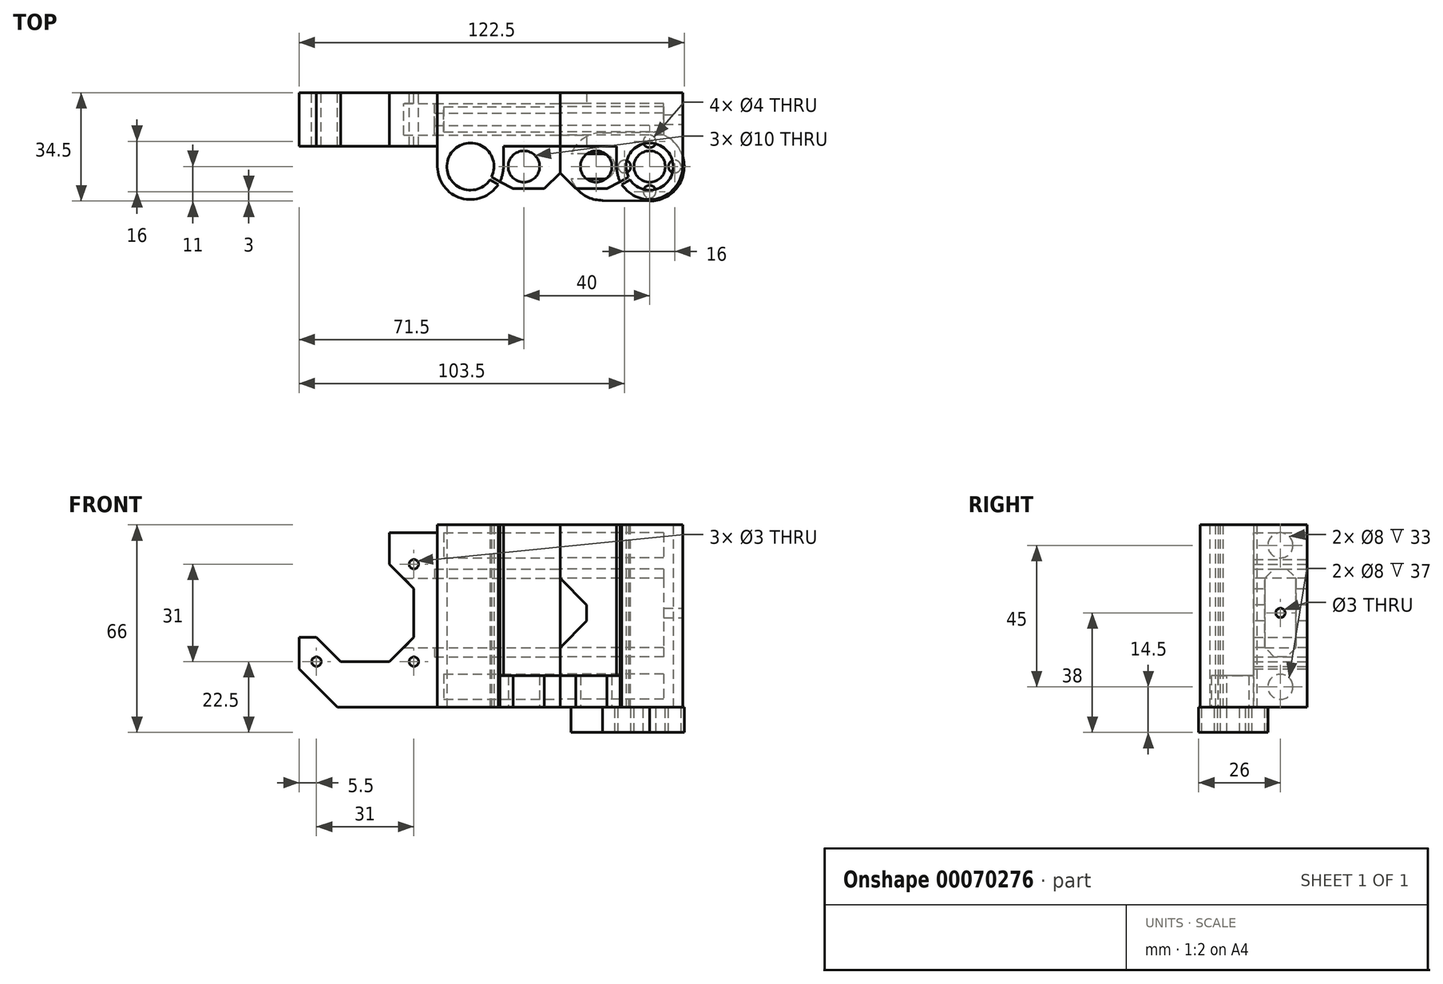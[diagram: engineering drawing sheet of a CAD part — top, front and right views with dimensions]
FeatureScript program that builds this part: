
annotation { "Feature Type Name" : "Feature", "Feature Type Description" : "" }
export const myFeature = defineFeature(function(context is Context, id is Id, definition is map)
    precondition{}
    {
        {
            var Q0;
            Q0=qCreatedBy(makeId("Top.planeOp"),FACE);
            var sketch = newSketch(context, id + "F0", { "sketchPlane" : qUnion([Q0])});
            skCircle(sketch, "E0", {"center": v(-17, 0) * mm, "radius": 5 * mm, "construction": true});
            skArc(sketch, "E1", {"start": v(-10.5, 0) * mm, "mid": v(-10.2, -2.48) * mm, "end": v(-9.33, -4.81) * mm});
            skLineSegment(sketch, "E2", {"start": v(-10.5, 0) * mm, "end": v(-10.5, 6.5) * mm});
            skLineSegment(sketch, "E3", {"start": v(-10.5, 6.5) * mm, "end": v(-28.5, 6.5) * mm});
            skLineSegment(sketch, "E4", {"start": v(-28.5, 6.5) * mm, "end": v(-28.5, 23.5) * mm});
            skLineSegment(sketch, "E5", {"start": v(-28.5, 23.5) * mm, "end": v(10.5, 23.5) * mm});
            skLineSegment(sketch, "E6", {"start": v(10.5, 23.5) * mm, "end": v(10.5, 0) * mm});
            skPoint(sketch, "E7", {"position": v(0, -10.5) * mm});
            skArc(sketch, "E8", {"start": v(-9.33, -4.81) * mm, "mid": v(-9.1, -5.25) * mm, "end": v(-8.83, -5.68) * mm});
            skArc(sketch, "E9", {"start": v(-6.73, -3.3) * mm, "mid": v(-6.5, -3.75) * mm, "end": v(-6.23, -4.17) * mm});
            skArc(sketch, "E10", {"start": v(-6.23, -4.17) * mm, "mid": v(6.5, 3.75) * mm, "end": v(-6.73, -3.3) * mm});
            skArc(sketch, "E11", {"start": v(-8.83, -5.68) * mm, "mid": v(2.96, -10.07) * mm, "end": v(10.5, 0) * mm});
            skLineSegment(sketch, "E12", {"start": v(-6.73, -3.3) * mm, "end": v(-9.33, -4.81) * mm});
            skLineSegment(sketch, "E13", {"start": v(-6.23, -4.17) * mm, "end": v(-8.83, -5.68) * mm});
            skLineSegment(sketch, "E14", {"start": v(0, 0) * mm, "end": v(-9.1, -5.25) * mm, "construction": true});
            skPoint(sketch, "E15", {"position": v(-6.5, -3.75) * mm});
            skSolve(sketch);
        }
        {
            var Q0;
            Q0=makeQuery(id+"F0.imprint","IMPRINT",FACE,{"disambiguationData":[TD([[makeQuery(id+"F0.imprint","IMPRINT",EDGE,{"derivedFrom":sQuery(id+"F0.wireOp",EDGE,"E1")}),1.0]])]});
            extrude(context, id + "F1", {"entities" : qUnion([Q0]), "depth" : 58 * mm});
        }
        {
            var Q0;
            Q0=makeQuery(id+"F1.opExtrude","SWEPT_FACE",FACE,{"disambiguationData":[OSD([sQuery(id+"F0.wireOp",EDGE,"E4")])]});
            var sketch = newSketch(context, id + "F2", { "sketchPlane" : qUnion([Q0])});
            skLineSegment(sketch, "E16", {"start": v(-15, 0) * mm, "end": v(-15, 58) * mm, "construction": true});
            skCircle(sketch, "E17", {"center": v(-15, 6.5) * mm, "radius": 4 * mm});
            skCircle(sketch, "E18", {"center": v(-15, 51.5) * mm, "radius": 4 * mm});
            skLineSegment(sketch, "E19", {"start": v(-23.5, 29) * mm, "end": v(-6.5, 29) * mm, "construction": true});
            skLineSegment(sketch, "E20", {"start": v(-20, 41) * mm, "end": v(-20, 19) * mm});
            skLineSegment(sketch, "E21", {"start": v(-20, 19) * mm, "end": v(-17, 16) * mm});
            skLineSegment(sketch, "E22", {"start": v(-17, 16) * mm, "end": v(-13, 16) * mm});
            skLineSegment(sketch, "E23", {"start": v(-13, 16) * mm, "end": v(-10, 19) * mm});
            skLineSegment(sketch, "E24", {"start": v(-10, 19) * mm, "end": v(-10, 41) * mm});
            skLineSegment(sketch, "E25", {"start": v(-10, 41) * mm, "end": v(-13, 44) * mm});
            skLineSegment(sketch, "E26", {"start": v(-13, 44) * mm, "end": v(-17, 44) * mm});
            skLineSegment(sketch, "E27", {"start": v(-17, 44) * mm, "end": v(-20, 41) * mm});
            skLineSegment(sketch, "E28", {"start": v(-20, 30) * mm, "end": v(-10, 30) * mm, "construction": true});
            skPoint(sketch, "E29", {"position": v(-15, 30) * mm});
            skCircle(sketch, "E30", {"center": v(-15, 30) * mm, "radius": 1.5 * mm, "construction": true});
            skSolve(sketch);
        }
        {
            var Q0;
            Q0=qCreatedBy(makeId("Top.planeOp"),FACE);
            var sketch = newSketch(context, id + "F3", { "sketchPlane" : qUnion([Q0])});
            skLineSegment(sketch, "E31.0", {"start": v(-10.5, 6.5) * mm, "end": v(-28.5, 6.5) * mm});
            skLineSegment(sketch, "E32.0", {"start": v(-10.5, 0) * mm, "end": v(-10.5, 6.5) * mm});
            skCircle(sketch, "E33.0", {"center": v(-17, 0) * mm, "radius": 5 * mm});
            skLineSegment(sketch, "E34", {"start": v(-28.5, 6.5) * mm, "end": v(-28.5, 6.5) * mm});
            skLineSegment(sketch, "E35", {"start": v(-28.5, 6.5) * mm, "end": v(-28.5, -7) * mm});
            skLineSegment(sketch, "E36", {"start": v(-28.5, -7) * mm, "end": v(-13.58, -7) * mm});
            skArc(sketch, "E37.0", {"start": v(-10.5, 0) * mm, "mid": v(-10.2, -2.48) * mm, "end": v(-9.33, -4.81) * mm});
            skLineSegment(sketch, "E38", {"start": v(-9.33, -4.81) * mm, "end": v(-13.58, -7) * mm});
            skSolve(sketch);
        }
        {
            var Q0;
            Q0=makeQuery(id+"F3.imprint","IMPRINT",FACE,{"disambiguationData":[TD([[makeQuery(id+"F3.imprint","IMPRINT",EDGE,{"derivedFrom":sQuery(id+"F3.wireOp",EDGE,"E31.0")}),1.0]])]});
            extrude(context, id + "F4", {"entities" : qUnion([Q0]), "operationType" : NewBodyOperationType.ADD, "depth" : 10 * mm});
        }
        {
            var Q0;
            Q0=makeQuery(id+"F4.opExtrude","SWEPT_EDGE",EDGE,{"disambiguationData":[OSD([sQuery(id+"F3.wireOp",EDGE,"E35"),sQuery(id+"F3.wireOp",EDGE,"E36")])]});
            chamfer(context, id + "F5", {"entities" : qUnion([Q0]), "width" : 5 * mm, "tangentPropagation" : true});
        }
        {
            var Q0;
            Q0=makeQuery(id+"F1.opExtrude","SWEPT_BODY",BODY,{"disambiguationData":[OSD([sQuery(id+"F0.wireOp",EDGE,"E1"),sQuery(id+"F0.wireOp",EDGE,"E2"),sQuery(id+"F0.wireOp",EDGE,"E3"),sQuery(id+"F0.wireOp",EDGE,"E4"),sQuery(id+"F0.wireOp",EDGE,"E5"),sQuery(id+"F0.wireOp",EDGE,"E6"),sQuery(id+"F0.wireOp",EDGE,"E10"),sQuery(id+"F0.wireOp",EDGE,"E11"),sQuery(id+"F0.wireOp",EDGE,"E12"),sQuery(id+"F0.wireOp",EDGE,"E13")])]});
            var Q1;
            Q1=makeQuery(id+"F1.opExtrude","SWEPT_FACE",FACE,{"disambiguationData":[OSD([sQuery(id+"F0.wireOp",EDGE,"E4")])]});
            mirror(context, id + "F6", {"entities" : qUnion([Q0]), "mirrorPlane" : qUnion([Q1])});
        }
        {
            var Q0;
            Q0=makeQuery(id+"F2.imprint","IMPRINT",FACE,{"disambiguationData":[TD([[makeQuery(id+"F2.imprint","IMPRINT",EDGE,{"derivedFrom":sQuery(id+"F2.wireOp",EDGE,"E20")}),1.0]])]});
            var Q1;
            Q1=makeQuery(id+"F2.imprint","IMPRINT",FACE,{"disambiguationData":[TD([[makeQuery(id+"F2.imprint","IMPRINT",EDGE,{"derivedFrom":sQuery(id+"F2.wireOp",EDGE,"E17")}),1.0]])]});
            var Q2;
            Q2=makeQuery(id+"F2.imprint","IMPRINT",FACE,{"disambiguationData":[TD([[makeQuery(id+"F2.imprint","IMPRINT",EDGE,{"derivedFrom":sQuery(id+"F2.wireOp",EDGE,"E30")}),1.0]])]});
            var Q3;
            Q3=makeQuery(id+"F2.imprint","IMPRINT",FACE,{"disambiguationData":[TD([[makeQuery(id+"F2.imprint","IMPRINT",EDGE,{"derivedFrom":sQuery(id+"F2.wireOp",EDGE,"E18")}),1.0]])]});
            extrude(context, id + "F7", {"entities" : qUnion([Q0, Q1, Q2, Q3]), "operationType" : NewBodyOperationType.REMOVE, "oppositeDirection" : true, "depth" : 33 * mm});
        }
        {
            var Q0;
            Q0=makeQuery(id+"F1.opExtrude","SWEPT_FACE",FACE,{"disambiguationData":[OSD([sQuery(id+"F0.wireOp",EDGE,"E6")])]});
            var sketch = newSketch(context, id + "F8", { "sketchPlane" : qUnion([Q0])});
            skCircle(sketch, "E39.0", {"center": v(15, 30) * mm, "radius": 1.5 * mm});
            skSolve(sketch);
        }
        {
            var Q0;
            Q0 = qSketchRegion(id + "F8", true);
            extrude(context, id + "F9", {"entities" : qUnion([Q0]), "operationType" : NewBodyOperationType.REMOVE, "endBound" : BoundingType.THROUGH_ALL, "oppositeDirection" : true, "depth" : 25 * mm});
        }
        {
            var Q0;
            Q0=makeQuery(id+"F2.imprint","IMPRINT",FACE,{"disambiguationData":[TD([[makeQuery(id+"F2.imprint","IMPRINT",EDGE,{"derivedFrom":sQuery(id+"F2.wireOp",EDGE,"E18")}),1.0]])]});
            var Q1;
            Q1=makeQuery(id+"F2.imprint","IMPRINT",FACE,{"disambiguationData":[TD([[makeQuery(id+"F2.imprint","IMPRINT",EDGE,{"derivedFrom":sQuery(id+"F2.wireOp",EDGE,"E17")}),1.0]])]});
            extrude(context, id + "F10", {"entities" : qUnion([Q0, Q1]), "operationType" : NewBodyOperationType.REMOVE, "depth" : 37 * mm});
        }
        {
            var Q0;
            Q0=makeQuery(id+"F6.opPattern","COPY",FACE,{"derivedFrom":makeQuery(id+"F1.opExtrude","SWEPT_FACE",FACE,{"disambiguationData":[OSD([sQuery(id+"F0.wireOp",EDGE,"E5")])]}),"instanceName":"1"});
            var sketch = newSketch(context, id + "F11", { "sketchPlane" : qUnion([Q0])});
            skPoint(sketch, "E40.0", {"position": v(28.5, 30) * mm});
            skLineSegment(sketch, "E41", {"start": v(28.5, 30) * mm, "end": v(132, 30) * mm, "construction": true});
            skLineSegment(sketch, "E42", {"start": v(67.5, 0) * mm, "end": v(99.25, 0) * mm});
            skLineSegment(sketch, "E43", {"start": v(99.25, 0) * mm, "end": v(111.5, 12.25) * mm});
            skLineSegment(sketch, "E44", {"start": v(111.5, 12.25) * mm, "end": v(111.5, 22.25) * mm});
            skLineSegment(sketch, "E45", {"start": v(111.5, 22.25) * mm, "end": v(106, 22.25) * mm});
            skLineSegment(sketch, "E46", {"start": v(106, 22.25) * mm, "end": v(98.25, 14.5) * mm});
            skLineSegment(sketch, "E47", {"start": v(98.25, 14.5) * mm, "end": v(82.75, 14.5) * mm});
            skLineSegment(sketch, "E48", {"start": v(82.75, 14.5) * mm, "end": v(75, 22.25) * mm});
            skLineSegment(sketch, "E49", {"start": v(75, 22.25) * mm, "end": v(75, 37.75) * mm});
            skLineSegment(sketch, "E50", {"start": v(75, 37.75) * mm, "end": v(82.75, 45.5) * mm});
            skLineSegment(sketch, "E51", {"start": v(82.75, 45.5) * mm, "end": v(82.75, 55.5) * mm});
            skLineSegment(sketch, "E52", {"start": v(82.75, 55.5) * mm, "end": v(67.5, 55.5) * mm});
            skLineSegment(sketch, "E53", {"start": v(90.5, 83.23) * mm, "end": v(90.5, 5.3) * mm, "construction": true});
            skCircle(sketch, "E54", {"center": v(90.5, 30) * mm, "radius": 11.5 * mm, "construction": true});
            skLineSegment(sketch, "E55.bottom", {"start": v(106, 45.5) * mm, "end": v(75, 45.5) * mm, "construction": true});
            skLineSegment(sketch, "E55.top", {"start": v(106, 14.5) * mm, "end": v(75, 14.5) * mm, "construction": true});
            skLineSegment(sketch, "E55.left", {"start": v(106, 45.5) * mm, "end": v(106, 14.5) * mm, "construction": true});
            skLineSegment(sketch, "E55.right", {"start": v(75, 45.5) * mm, "end": v(75, 14.5) * mm, "construction": true});
            skPoint(sketch, "E56", {"position": v(106, 30) * mm});
            skPoint(sketch, "E57", {"position": v(75, 30) * mm});
            skPoint(sketch, "E58", {"position": v(90.5, 45.5) * mm});
            skPoint(sketch, "E59", {"position": v(90.5, 14.5) * mm});
            skLineSegment(sketch, "E60", {"start": v(90.5, 45.5) * mm, "end": v(90.5, 14.5) * mm, "construction": true});
            skLineSegment(sketch, "E61", {"start": v(106, 30) * mm, "end": v(75, 30) * mm, "construction": true});
            skCircle(sketch, "E62", {"center": v(106, 45.5) * mm, "radius": 1.5 * mm, "construction": true});
            skCircle(sketch, "E63", {"center": v(75, 45.5) * mm, "radius": 1.5 * mm});
            skCircle(sketch, "E64", {"center": v(75, 14.5) * mm, "radius": 1.5 * mm});
            skCircle(sketch, "E65", {"center": v(106, 14.5) * mm, "radius": 1.5 * mm});
            skLineSegment(sketch, "E66.bottom", {"start": v(111.5, 51) * mm, "end": v(69.5, 51) * mm, "construction": true});
            skLineSegment(sketch, "E66.top", {"start": v(111.5, 9) * mm, "end": v(69.5, 9) * mm, "construction": true});
            skLineSegment(sketch, "E66.left", {"start": v(111.5, 51) * mm, "end": v(111.5, 9) * mm, "construction": true});
            skLineSegment(sketch, "E66.right", {"start": v(69.5, 51) * mm, "end": v(69.5, 9) * mm, "construction": true});
            skPoint(sketch, "E67", {"position": v(90.5, 51) * mm});
            skPoint(sketch, "E68", {"position": v(69.5, 30) * mm});
            skLineSegment(sketch, "E69", {"start": v(90.5, 30) * mm, "end": v(102.12, 18.38) * mm, "construction": true});
            skLineSegment(sketch, "E70", {"start": v(90.5, 30) * mm, "end": v(78.88, 18.38) * mm, "construction": true});
            skLineSegment(sketch, "E71", {"start": v(90.5, 30) * mm, "end": v(78.88, 41.63) * mm, "construction": true});
            skPoint(sketch, "E72", {"position": v(75, 37.75) * mm});
            skLineSegment(sketch, "E73", {"start": v(75, 30) * mm, "end": v(75, 45.5) * mm, "construction": true});
            skLineSegment(sketch, "E74", {"start": v(106, 14.5) * mm, "end": v(102.12, 18.38) * mm});
            skLineSegment(sketch, "E75", {"start": v(106, 14.5) * mm, "end": v(109.88, 10.62) * mm, "construction": true});
            skSolve(sketch);
        }
        {
            var Q0;
            {var subQ4=sQuery(id+"F11.wireOp",EDGE,"E42");Q0=makeQuery(id+"F11.imprint","IMPRINT",FACE,{"disambiguationData":[TD([[makeQuery(id+"F11.imprint","IMPRINT",EDGE,{"derivedFrom":subQ4}),1.0]])]});}
            extrude(context, id + "F12", {"entities" : qUnion([Q0]), "operationType" : NewBodyOperationType.ADD, "oppositeDirection" : true, "depth" : 17 * mm});
        }
        {
            var Q0;
            Q0=makeQuery(id+"F2.imprint","IMPRINT",FACE,{"disambiguationData":[TD([[makeQuery(id+"F2.imprint","IMPRINT",EDGE,{"derivedFrom":sQuery(id+"F2.wireOp",EDGE,"E20")}),1.0]])]});
            var Q1;
            Q1=makeQuery(id+"F6.opPattern","COPY",FACE,{"derivedFrom":makeQuery(id+"F1.opExtrude","SWEPT_FACE",FACE,{"disambiguationData":[OSD([sQuery(id+"F0.wireOp",EDGE,"E6")])]}),"instanceName":"1"});
            extrude(context, id + "F13", {"entities" : qUnion([Q0]), "operationType" : NewBodyOperationType.REMOVE, "endBoundEntityFace" : qUnion([Q1]), "depth" : 40 * mm});
        }
        {
            var Q0;
            Q0=makeQuery(id+"F13.boolean.opBoolean","COPY",FACE,{"derivedFrom":makeQuery(id+"F13.opExtrude","CAP_FACE",FACE,{"disambiguationData":[OSD([sQuery(id+"F2.wireOp",EDGE,"E20"),sQuery(id+"F2.wireOp",EDGE,"E21"),sQuery(id+"F2.wireOp",EDGE,"E22"),sQuery(id+"F2.wireOp",EDGE,"E23"),sQuery(id+"F2.wireOp",EDGE,"E24"),sQuery(id+"F2.wireOp",EDGE,"E25"),sQuery(id+"F2.wireOp",EDGE,"E26"),sQuery(id+"F2.wireOp",EDGE,"E27")])],"isStart":false})});
            var sketch = newSketch(context, id + "F14", { "sketchPlane" : qUnion([Q0])});
            skLineSegment(sketch, "E76.0", {"start": v(10, 19) * mm, "end": v(10, 41) * mm});
            skLineSegment(sketch, "E77.0", {"start": v(20, 41) * mm, "end": v(20, 19) * mm});
            skLineSegment(sketch, "E78", {"start": v(20, 41) * mm, "end": v(10, 41) * mm});
            skLineSegment(sketch, "E79", {"start": v(20, 19) * mm, "end": v(10, 19) * mm});
            skSolve(sketch);
        }
        {
            var Q0;
            Q0=makeQuery(id+"F14.imprint","IMPRINT",FACE,{"disambiguationData":[TD([[makeQuery(id+"F14.imprint","IMPRINT",EDGE,{"derivedFrom":sQuery(id+"F14.wireOp",EDGE,"E76.0")}),-1.0]])]});
            var Q1;
            Q1=makeQuery(id+"F12.opExtrude","SWEPT_FACE",FACE,{"disambiguationData":[OSD([sQuery(id+"F11.wireOp",EDGE,"E46")])]});
            extrude(context, id + "F15", {"entities" : qUnion([Q0]), "operationType" : NewBodyOperationType.REMOVE, "endBound" : BoundingType.UP_TO_SURFACE, "oppositeDirection" : true, "endBoundEntityFace" : qUnion([Q1]), "depth" : 25 * mm});
        }
        {
            var Q0;
            Q0=makeQuery(id+"F1.opExtrude","SWEPT_FACE",FACE,{"disambiguationData":[OSD([sQuery(id+"F0.wireOp",EDGE,"E3")])]});
            var sketch = newSketch(context, id + "F16", { "sketchPlane" : qUnion([Q0])});
            skPoint(sketch, "E80.0", {"position": v(-28.5, 30) * mm});
            skLineSegment(sketch, "E81", {"start": v(-28.5, 30) * mm, "end": v(-10.5, 30) * mm, "construction": true});
            skPoint(sketch, "E82.0", {"position": v(-28.5, 41) * mm});
            skPoint(sketch, "E83.0", {"position": v(-28.5, 19) * mm});
            skLineSegment(sketch, "E84", {"start": v(-28.5, 41) * mm, "end": v(-20.03, 32.5) * mm});
            skLineSegment(sketch, "E85", {"start": v(-20.03, 32.5) * mm, "end": v(-20.03, 27.5) * mm});
            skLineSegment(sketch, "E86", {"start": v(-20.03, 27.5) * mm, "end": v(-28.5, 19) * mm});
            skSolve(sketch);
        }
        {
            var Q0;
            {var subQ0=sQuery(id+"F16.wireOp",EDGE,"E84");Q0=makeQuery(id+"F16.imprint","IMPRINT",FACE,{"disambiguationData":[TD([[makeQuery(id+"F16.imprint","IMPRINT",EDGE,{"derivedFrom":subQ0}),-1.0]])]});}
            extrude(context, id + "F17", {"entities" : qUnion([Q0]), "operationType" : NewBodyOperationType.REMOVE, "endBound" : BoundingType.THROUGH_ALL, "oppositeDirection" : true, "depth" : 25 * mm});
        }
        {
            var Q0;
            Q0=qCreatedBy(makeId("Top.planeOp"),FACE);
            var sketch = newSketch(context, id + "F18", { "sketchPlane" : qUnion([Q0])});
            skPoint(sketch, "E87.0", {"position": v(0, 0) * mm});
            skLineSegment(sketch, "E88", {"start": v(0, 0) * mm, "end": v(-15, 0) * mm, "construction": true});
            skLineSegment(sketch, "E89", {"start": v(0, -5) * mm, "end": v(-15, -4) * mm, "construction": true});
            skLineSegment(sketch, "E90", {"start": v(-15, 4) * mm, "end": v(0, 5) * mm, "construction": true});
            skArc(sketch, "E91", {"start": v(-15, -4) * mm, "mid": v(-11, 0) * mm, "end": v(-15, 4) * mm});
            skArc(sketch, "E92", {"start": v(0, -5) * mm, "mid": v(5, 0) * mm, "end": v(0, 5) * mm});
            skArc(sketch, "E93", {"start": v(0, 5) * mm, "mid": v(-5, 0) * mm, "end": v(0, -5) * mm});
            skArc(sketch, "E94.0", {"start": v(0, -11) * mm, "mid": v(11, 0) * mm, "end": v(0, 11) * mm});
            skLineSegment(sketch, "E94.1", {"start": v(0, -11) * mm, "end": v(-15, -10.77) * mm});
            skArc(sketch, "E94.2", {"start": v(-15, 10.77) * mm, "mid": v(-21.04, 8.92) * mm, "end": v(-25, 4) * mm});
            skLineSegment(sketch, "E94.3", {"start": v(-15, 10.77) * mm, "end": v(0, 11) * mm});
            skLineSegment(sketch, "E95", {"start": v(-15, -4) * mm, "end": v(-25, -4) * mm});
            skLineSegment(sketch, "E96", {"start": v(-15, 4) * mm, "end": v(-25, 4) * mm});
            skArc(sketch, "E97", {"start": v(-25, -4) * mm, "mid": v(-21.04, -8.92) * mm, "end": v(-15, -10.77) * mm});
            skCircle(sketch, "E98", {"center": v(0, 8) * mm, "radius": 2 * mm});
            skCircle(sketch, "E99", {"center": v(8, 0) * mm, "radius": 2 * mm});
            skCircle(sketch, "E100", {"center": v(0, -8) * mm, "radius": 2 * mm});
            skCircle(sketch, "E101", {"center": v(-8, 0) * mm, "radius": 2 * mm});
            skPoint(sketch, "E102", {"position": v(-7.5, 0) * mm});
            skSolve(sketch);
        }
        {
            var Q0;
            Q0=makeQuery(id+"F18.imprint","IMPRINT",FACE,{"disambiguationData":[TD([[makeQuery(id+"F18.imprint","IMPRINT",EDGE,{"derivedFrom":sQuery(id+"F18.wireOp",EDGE,"E91")}),-1.0]])]});
            extrude(context, id + "F19", {"entities" : qUnion([Q0]), "oppositeDirection" : true, "depth" : 8 * mm});
        }
    });
